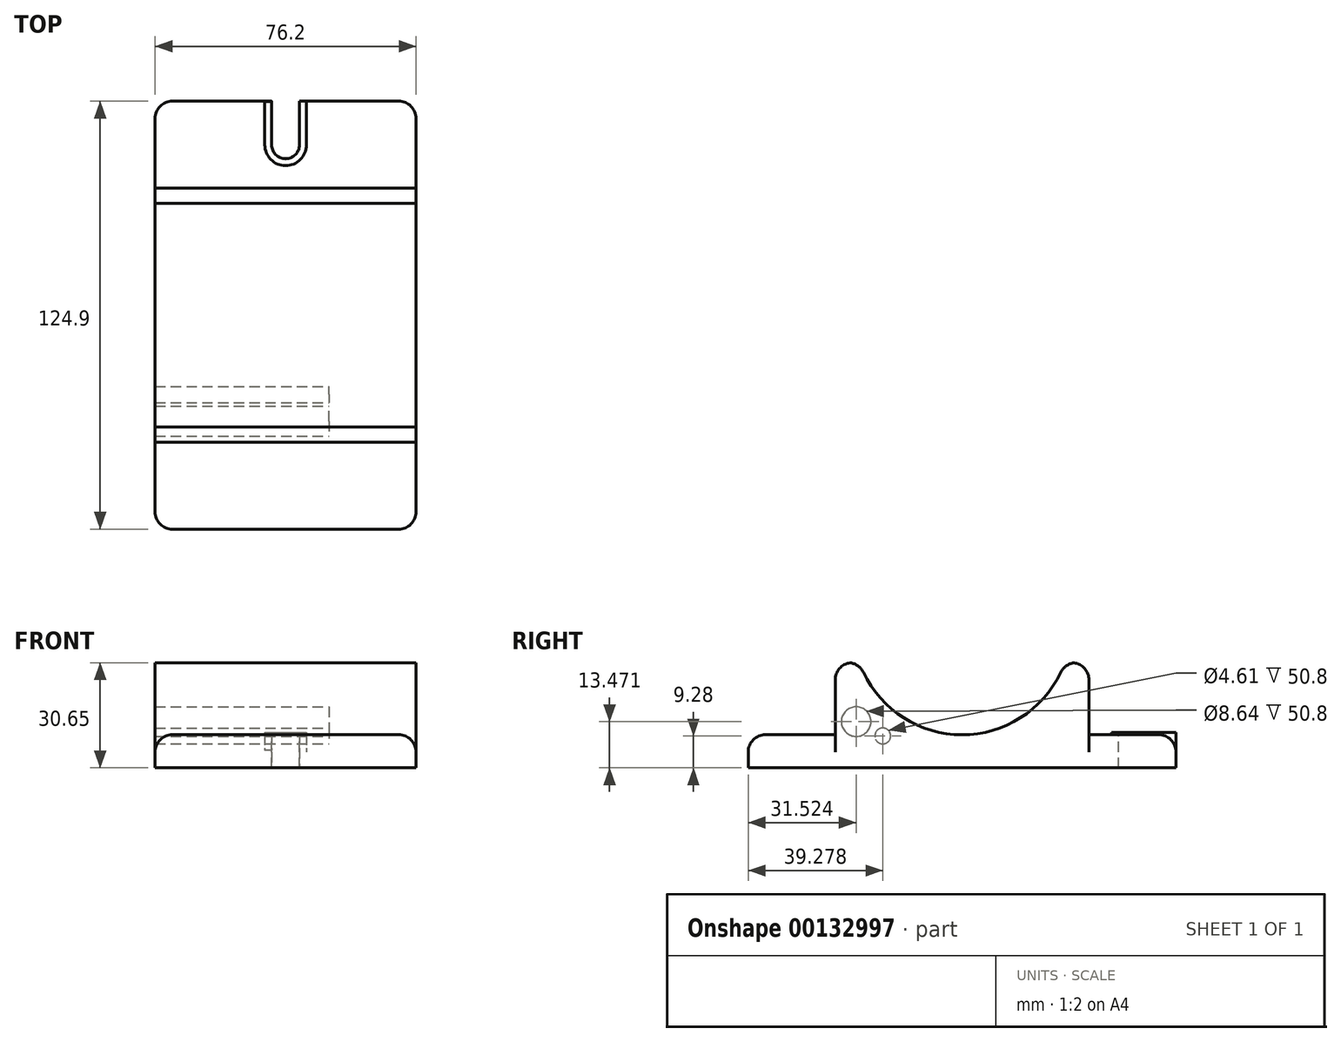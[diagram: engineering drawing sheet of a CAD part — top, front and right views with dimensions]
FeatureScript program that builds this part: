
annotation { "Feature Type Name" : "Feature", "Feature Type Description" : "" }
export const myFeature = defineFeature(function(context is Context, id is Id, definition is map)
    precondition{}
    {
        {
            var Q0;
            Q0=qCreatedBy(makeId("Right.planeOp"),FACE);
            var sketch = newSketch(context, id + "F0", { "sketchPlane" : qUnion([Q0])});
            skArc(sketch, "E0", {"start": v(-30, -2.7) * mm, "mid": v(0, -23.75) * mm, "end": v(30, -2.7) * mm});
            skLineSegment(sketch, "E1", {"start": v(-30, -2.7) * mm, "end": v(-37.05, -2.7) * mm});
            skLineSegment(sketch, "E2", {"start": v(-37.05, -2.7) * mm, "end": v(-37.05, -23.76) * mm});
            skLineSegment(sketch, "E3", {"start": v(-37.05, -23.76) * mm, "end": v(0, -23.75) * mm});
            skLineSegment(sketch, "E4", {"start": v(0, -23.75) * mm, "end": v(37.05, -23.75) * mm});
            skLineSegment(sketch, "E5", {"start": v(30, -2.7) * mm, "end": v(37.05, -2.7) * mm});
            skLineSegment(sketch, "E6", {"start": v(37.05, -2.7) * mm, "end": v(37.05, -23.75) * mm});
            skLineSegment(sketch, "E7.bottom", {"start": v(-62.45, -23.75) * mm, "end": v(62.45, -23.75) * mm});
            skLineSegment(sketch, "E7.top", {"start": v(-62.45, -33.4) * mm, "end": v(62.45, -33.4) * mm});
            skLineSegment(sketch, "E7.left", {"start": v(-62.45, -23.75) * mm, "end": v(-62.45, -33.4) * mm});
            skLineSegment(sketch, "E7.right", {"start": v(62.45, -23.75) * mm, "end": v(62.45, -33.4) * mm});
            skSolve(sketch);
        }
        {
            var Q0;
            Q0 = qSketchRegion(id + "F0", true);
            extrude(context, id + "F1", {"entities" : qUnion([Q0]), "depth" : 38.1 * mm, "hasSecondDirection" : true, "secondDirectionOppositeDirection" : true, "secondDirectionDepth" : 38.1 * mm});
        }
        {
            var Q0;
            Q0=qCreatedBy(makeId("Top.planeOp"),FACE);
            var sketch = newSketch(context, id + "F2", { "sketchPlane" : qUnion([Q0])});
            skArc(sketch, "E8", {"start": v(-4.06, 49.75) * mm, "mid": v(0, 45.69) * mm, "end": v(4.06, 49.75) * mm});
            skLineSegment(sketch, "E9", {"start": v(4.06, 49.75) * mm, "end": v(4.06, 62.5) * mm});
            skLineSegment(sketch, "E10", {"start": v(-4.06, 49.75) * mm, "end": v(-4.06, 62.45) * mm});
            skLineSegment(sketch, "E11", {"start": v(-4.06, 62.45) * mm, "end": v(4.06, 62.5) * mm});
            skSolve(sketch);
        }
        {
            var Q0;
            Q0=makeQuery(id+"F2.imprint","IMPRINT",FACE,{"disambiguationData":[TD([[makeQuery(id+"F2.imprint","IMPRINT",EDGE,{"derivedFrom":sQuery(id+"F2.wireOp",EDGE,"E8")}),1.0]])]});
            extrude(context, id + "F3", {"entities" : qUnion([Q0]), "operationType" : NewBodyOperationType.REMOVE, "oppositeDirection" : true, "depth" : 50.8 * mm});
        }
        {
            var Q0;
            Q0=makeQuery(id+"F1.opExtrude","SWEPT_EDGE",EDGE,{"disambiguationData":[OSD([sQuery(id+"F0.wireOp",EDGE,"E5"),sQuery(id+"F0.wireOp",EDGE,"E6")])]});
            var Q1;
            Q1=makeQuery(id+"F1.opExtrude","SWEPT_EDGE",EDGE,{"disambiguationData":[OSD([sQuery(id+"F0.wireOp",EDGE,"E0"),sQuery(id+"F0.wireOp",EDGE,"E5")])]});
            var Q2;
            Q2=makeQuery(id+"F1.opExtrude","SWEPT_EDGE",EDGE,{"disambiguationData":[OSD([sQuery(id+"F0.wireOp",EDGE,"E0"),sQuery(id+"F0.wireOp",EDGE,"E1")])]});
            var Q3;
            Q3=makeQuery(id+"F1.opExtrude","SWEPT_EDGE",EDGE,{"disambiguationData":[OSD([sQuery(id+"F0.wireOp",EDGE,"E1"),sQuery(id+"F0.wireOp",EDGE,"E2")])]});
            var Q4;
            {var subQ0=sQuery(id+"F0.wireOp",EDGE,"E7.bottom");Q4=makeQuery(id+"F1.opExtrude","CAP_EDGE",EDGE,{"disambiguationData":[OSD([subQ0]),TDD([makeQuery(id+"F0.imprint","IMPRINT",EDGE,{"disambiguationData":[TD([[makeQuery(id+"F0.imprint","INTERSECT",VERTEX,{"derivedFrom":[sQuery(id+"F0.wireOp",EDGE,"E6"),subQ0]}),-1.0]])],"derivedFrom":subQ0})])],"isStart":true});}
            var Q5;
            {var subQ0=sQuery(id+"F0.wireOp",EDGE,"E7.right");var subQ1=sQuery(id+"F0.wireOp",EDGE,"E7.bottom");Q5=makeQuery(id+"F3.boolean.opBoolean","SPLIT",EDGE,{"disambiguationData":[TD([makeQuery(id+"F3.opExtrude","SWEPT_FACE",FACE,{"disambiguationData":[OSD([sQuery(id+"F2.wireOp",EDGE,"E10")])]})])],"derivedFrom":makeQuery(id+"F1.opExtrude","SWEPT_EDGE",EDGE,{"disambiguationData":[OSD([subQ1,subQ0])]})});}
            var Q6;
            Q6=makeQuery(id+"F1.opExtrude","CAP_EDGE",EDGE,{"disambiguationData":[OSD([sQuery(id+"F0.wireOp",EDGE,"E7.right")])],"isStart":true});
            var Q7;
            {var subQ0=sQuery(id+"F0.wireOp",EDGE,"E7.right");var subQ1=sQuery(id+"F0.wireOp",EDGE,"E7.bottom");Q7=makeQuery(id+"F3.boolean.opBoolean","SPLIT",EDGE,{"disambiguationData":[TD([makeQuery(id+"F3.opExtrude","SWEPT_FACE",FACE,{"disambiguationData":[OSD([sQuery(id+"F2.wireOp",EDGE,"E9")])]})])],"derivedFrom":makeQuery(id+"F1.opExtrude","SWEPT_EDGE",EDGE,{"disambiguationData":[OSD([subQ1,subQ0])]})});}
            var Q8;
            {var subQ0=sQuery(id+"F0.wireOp",EDGE,"E7.bottom");Q8=makeQuery(id+"F1.opExtrude","CAP_EDGE",EDGE,{"disambiguationData":[OSD([subQ0]),TDD([makeQuery(id+"F0.imprint","IMPRINT",EDGE,{"disambiguationData":[TD([[makeQuery(id+"F0.imprint","INTERSECT",VERTEX,{"derivedFrom":[sQuery(id+"F0.wireOp",EDGE,"E6"),subQ0]}),-1.0]])],"derivedFrom":subQ0})])],"isStart":false});}
            var Q9;
            Q9=makeQuery(id+"F1.opExtrude","CAP_EDGE",EDGE,{"disambiguationData":[OSD([sQuery(id+"F0.wireOp",EDGE,"E7.right")])],"isStart":false});
            var Q10;
            Q10=makeQuery(id+"F1.opExtrude","CAP_EDGE",EDGE,{"disambiguationData":[OSD([sQuery(id+"F0.wireOp",EDGE,"E7.left")])],"isStart":false});
            var Q11;
            Q11=makeQuery(id+"F1.opExtrude","CAP_EDGE",EDGE,{"disambiguationData":[OSD([sQuery(id+"F0.wireOp",EDGE,"E7.left")])],"isStart":true});
            var Q12;
            {var subQ0=sQuery(id+"F0.wireOp",EDGE,"E7.left");var subQ1=sQuery(id+"F0.wireOp",EDGE,"E7.bottom");Q12=makeQuery(id+"FwKWZMWK3dbIE5p_3.1.F3.boolean.opBoolean","SPLIT",EDGE,{"disambiguationData":[TD([makeQuery(id+"FwKWZMWK3dbIE5p_3.1.F3.opExtrude","SWEPT_FACE",FACE,{"disambiguationData":[OSD([sQuery(id+"F2.wireOp",EDGE,"E9")])]})])],"derivedFrom":makeQuery(id+"F1.opExtrude","SWEPT_EDGE",EDGE,{"disambiguationData":[OSD([subQ1,subQ0])]})});}
            var Q13;
            {var subQ0=sQuery(id+"F0.wireOp",EDGE,"E7.bottom");Q13=makeQuery(id+"F1.opExtrude","CAP_EDGE",EDGE,{"disambiguationData":[OSD([subQ0]),TDD([makeQuery(id+"F0.imprint","IMPRINT",EDGE,{"disambiguationData":[TD([[makeQuery(id+"F0.imprint","INTERSECT",VERTEX,{"derivedFrom":[subQ0,sQuery(id+"F0.wireOp",EDGE,"E7.left")]}),-1.0]])],"derivedFrom":subQ0})])],"isStart":false});}
            var Q14;
            {var subQ0=sQuery(id+"F0.wireOp",EDGE,"E7.left");var subQ1=sQuery(id+"F0.wireOp",EDGE,"E7.bottom");Q14=makeQuery(id+"FwKWZMWK3dbIE5p_3.1.F3.boolean.opBoolean","SPLIT",EDGE,{"disambiguationData":[TD([makeQuery(id+"FwKWZMWK3dbIE5p_3.1.F3.opExtrude","SWEPT_FACE",FACE,{"disambiguationData":[OSD([sQuery(id+"F2.wireOp",EDGE,"E10")])]})])],"derivedFrom":makeQuery(id+"F1.opExtrude","SWEPT_EDGE",EDGE,{"disambiguationData":[OSD([subQ1,subQ0])]})});}
            var Q15;
            {var subQ0=sQuery(id+"F0.wireOp",EDGE,"E7.bottom");Q15=makeQuery(id+"F1.opExtrude","CAP_EDGE",EDGE,{"disambiguationData":[OSD([subQ0]),TDD([makeQuery(id+"F0.imprint","IMPRINT",EDGE,{"disambiguationData":[TD([[makeQuery(id+"F0.imprint","INTERSECT",VERTEX,{"derivedFrom":[subQ0,sQuery(id+"F0.wireOp",EDGE,"E7.left")]}),-1.0]])],"derivedFrom":subQ0})])],"isStart":true});}
            fillet(context, id + "F4", {"entities" : qUnion([Q0, Q1, Q2, Q3, Q4, Q5, Q6, Q7, Q8, Q9, Q10, Q11, Q12, Q13, Q14, Q15]), "radius" : 5.08 * mm, "tangentPropagation" : true, "allowEdgeOverflow" : false});
        }
        {
            var Q0;
            Q0=qCreatedBy(makeId("Top.planeOp"),FACE);
            var sketch = newSketch(context, id + "F5", { "sketchPlane" : qUnion([Q0])});
            skArc(sketch, "E12", {"start": v(-4.06, 49.71) * mm, "mid": v(0, 45.65) * mm, "end": v(4.06, 49.71) * mm});
            skLineSegment(sketch, "E13", {"start": v(4.06, 49.71) * mm, "end": v(4.06, 62.45) * mm});
            skLineSegment(sketch, "E14", {"start": v(-4.06, 49.71) * mm, "end": v(-4.06, 62.42) * mm});
            skLineSegment(sketch, "E15.0", {"start": v(6.06, 49.71) * mm, "end": v(6.06, 62.45) * mm});
            skLineSegment(sketch, "E16.0", {"start": v(-6.06, 49.71) * mm, "end": v(-6.06, 62.42) * mm});
            skLineSegment(sketch, "E17", {"start": v(-6.06, 62.42) * mm, "end": v(-4.06, 62.42) * mm});
            skLineSegment(sketch, "E18", {"start": v(4.06, 62.45) * mm, "end": v(6.06, 62.45) * mm});
            skArc(sketch, "E19", {"start": v(-6.06, 49.71) * mm, "mid": v(0, 43.65) * mm, "end": v(6.06, 49.71) * mm});
            skSolve(sketch);
        }
        {
            var Q0;
            Q0=qCreatedBy(makeId("Top.planeOp"),FACE);
            cPlane(context, id + "F6", {"entities" : qUnion([Q0]), "cplaneType" : CPlaneType.OFFSET, "offset" : 30.7 * mm, "oppositeDirection" : true, "width" : 152.4 * mm, "height" : 152.4 * mm});
        }
        {
            var Q0;
            Q0=qCreatedBy(id+"F6.planeOp",FACE);
            var sketch = newSketch(context, id + "F7", { "sketchPlane" : qUnion([Q0])});
            skArc(sketch, "E20", {"start": v(-4.06, 49.71) * mm, "mid": v(0, 45.65) * mm, "end": v(4.06, 49.71) * mm});
            skLineSegment(sketch, "E21", {"start": v(4.06, 49.71) * mm, "end": v(4.06, 62.45) * mm});
            skLineSegment(sketch, "E22", {"start": v(-4.06, 49.71) * mm, "end": v(-4.06, 62.42) * mm});
            skLineSegment(sketch, "E23.0", {"start": v(6.06, 49.71) * mm, "end": v(6.06, 62.45) * mm});
            skLineSegment(sketch, "E24.0", {"start": v(-6.06, 49.71) * mm, "end": v(-6.06, 62.42) * mm});
            skLineSegment(sketch, "E25", {"start": v(-6.06, 62.42) * mm, "end": v(-4.06, 62.42) * mm});
            skLineSegment(sketch, "E26", {"start": v(4.06, 62.45) * mm, "end": v(6.06, 62.45) * mm});
            skArc(sketch, "E27", {"start": v(-6.06, 49.71) * mm, "mid": v(0, 43.65) * mm, "end": v(6.06, 49.71) * mm});
            skSolve(sketch);
        }
        {
            var Q0;
            Q0 = qSketchRegion(id + "F7", true);
            extrude(context, id + "F8", {"entities" : qUnion([Q0]), "operationType" : NewBodyOperationType.ADD, "depth" : 7.62 * mm});
        }
        {
            var Q0;
            Q0=makeQuery(id+"F1.opExtrude","CAP_FACE",FACE,{"disambiguationData":[OSD([sQuery(id+"F0.wireOp",EDGE,"E0"),sQuery(id+"F0.wireOp",EDGE,"E1"),sQuery(id+"F0.wireOp",EDGE,"E2"),sQuery(id+"F0.wireOp",EDGE,"E5"),sQuery(id+"F0.wireOp",EDGE,"E6"),sQuery(id+"F0.wireOp",EDGE,"E7.bottom"),sQuery(id+"F0.wireOp",EDGE,"E7.top"),sQuery(id+"F0.wireOp",EDGE,"E7.left"),sQuery(id+"F0.wireOp",EDGE,"E7.right")])],"isStart":true});
            var sketch = newSketch(context, id + "F9", { "sketchPlane" : qUnion([Q0])});
            skCircle(sketch, "E28", {"center": v(30.93, -19.92) * mm, "radius": 4.32 * mm});
            skCircle(sketch, "E29", {"center": v(23.17, -24.11) * mm, "radius": 2.3 * mm});
            skSolve(sketch);
        }
        {
            var Q0;
            Q0 = qSketchRegion(id + "F9", true);
            extrude(context, id + "F10", {"entities" : qUnion([Q0]), "operationType" : NewBodyOperationType.REMOVE, "depth" : 25.4 * mm, "hasSecondDirection" : true, "secondDirectionOppositeDirection" : true, "secondDirectionDepth" : 50.8 * mm});
        }
    });
